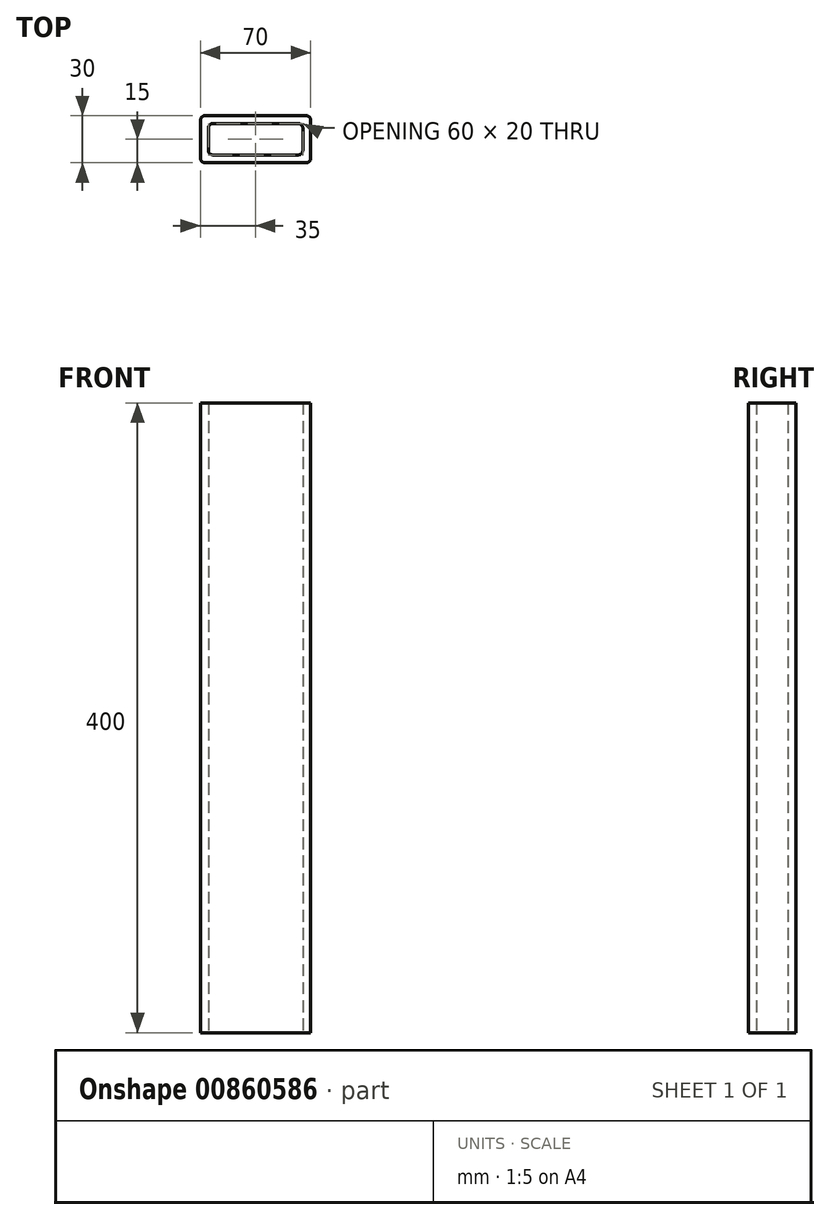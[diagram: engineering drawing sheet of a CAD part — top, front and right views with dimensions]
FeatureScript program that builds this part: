
annotation { "Feature Type Name" : "Feature", "Feature Type Description" : "" }
export const myFeature = defineFeature(function(context is Context, id is Id, definition is map)
    precondition{}
    {
        {
            var Q0;
            Q0=qCreatedBy(makeId("Top.planeOp"),FACE);
            var sketch = newSketch(context, id + "F0", { "sketchPlane" : qUnion([Q0])});
            skLineSegment(sketch, "E0.bottom", {"start": v(32, 15) * mm, "end": v(-32, 15) * mm});
            skLineSegment(sketch, "E0.top", {"start": v(32, -15) * mm, "end": v(-32, -15) * mm});
            skLineSegment(sketch, "E0.left", {"start": v(35, 12) * mm, "end": v(35, -12) * mm});
            skLineSegment(sketch, "E0.right", {"start": v(-35, 12) * mm, "end": v(-35, -12) * mm});
            skPoint(sketch, "E0.middle", {"position": v(0, 0) * mm});
            skLineSegment(sketch, "E1.bottom", {"start": v(27, 10) * mm, "end": v(-27, 10) * mm});
            skLineSegment(sketch, "E1.top", {"start": v(27, -10) * mm, "end": v(-27, -10) * mm});
            skLineSegment(sketch, "E1.left", {"start": v(30, 7) * mm, "end": v(30, -7) * mm});
            skLineSegment(sketch, "E1.right", {"start": v(-30, 7) * mm, "end": v(-30, -7) * mm});
            skPoint(sketch, "E2.visualSharp", {"position": v(-35, 15) * mm});
            skArc(sketch, "E2.filletArc", {"start": v(-32, 15) * mm, "mid": v(-34.12, 14.12) * mm, "end": v(-35, 12) * mm});
            skPoint(sketch, "E3.visualSharp", {"position": v(35, 15) * mm});
            skArc(sketch, "E3.filletArc", {"start": v(35, 12) * mm, "mid": v(34.12, 14.12) * mm, "end": v(32, 15) * mm});
            skPoint(sketch, "E4.visualSharp", {"position": v(35, -15) * mm});
            skArc(sketch, "E4.filletArc", {"start": v(32, -15) * mm, "mid": v(34.12, -14.12) * mm, "end": v(35, -12) * mm});
            skPoint(sketch, "E5.visualSharp", {"position": v(-35, -15) * mm});
            skArc(sketch, "E5.filletArc", {"start": v(-35, -12) * mm, "mid": v(-34.12, -14.12) * mm, "end": v(-32, -15) * mm});
            skPoint(sketch, "E6.visualSharp", {"position": v(30, 10) * mm});
            skArc(sketch, "E6.filletArc", {"start": v(30, 7) * mm, "mid": v(29.12, 9.12) * mm, "end": v(27, 10) * mm});
            skPoint(sketch, "E7.visualSharp", {"position": v(30, -10) * mm});
            skArc(sketch, "E7.filletArc", {"start": v(27, -10) * mm, "mid": v(29.12, -9.12) * mm, "end": v(30, -7) * mm});
            skPoint(sketch, "E8.visualSharp", {"position": v(-30, -10) * mm});
            skArc(sketch, "E8.filletArc", {"start": v(-30, -7) * mm, "mid": v(-29.12, -9.12) * mm, "end": v(-27, -10) * mm});
            skPoint(sketch, "E9.visualSharp", {"position": v(-30, 10) * mm});
            skArc(sketch, "E9.filletArc", {"start": v(-27, 10) * mm, "mid": v(-29.12, 9.12) * mm, "end": v(-30, 7) * mm});
            skSolve(sketch);
        }
        {
            var Q0;
            Q0 = qSketchRegion(id + "F0", true);
            extrude(context, id + "F1", {"entities" : qUnion([Q0]), "depth" : 400 * mm, "offsetDistance" : 25 * mm});
        }
    });
